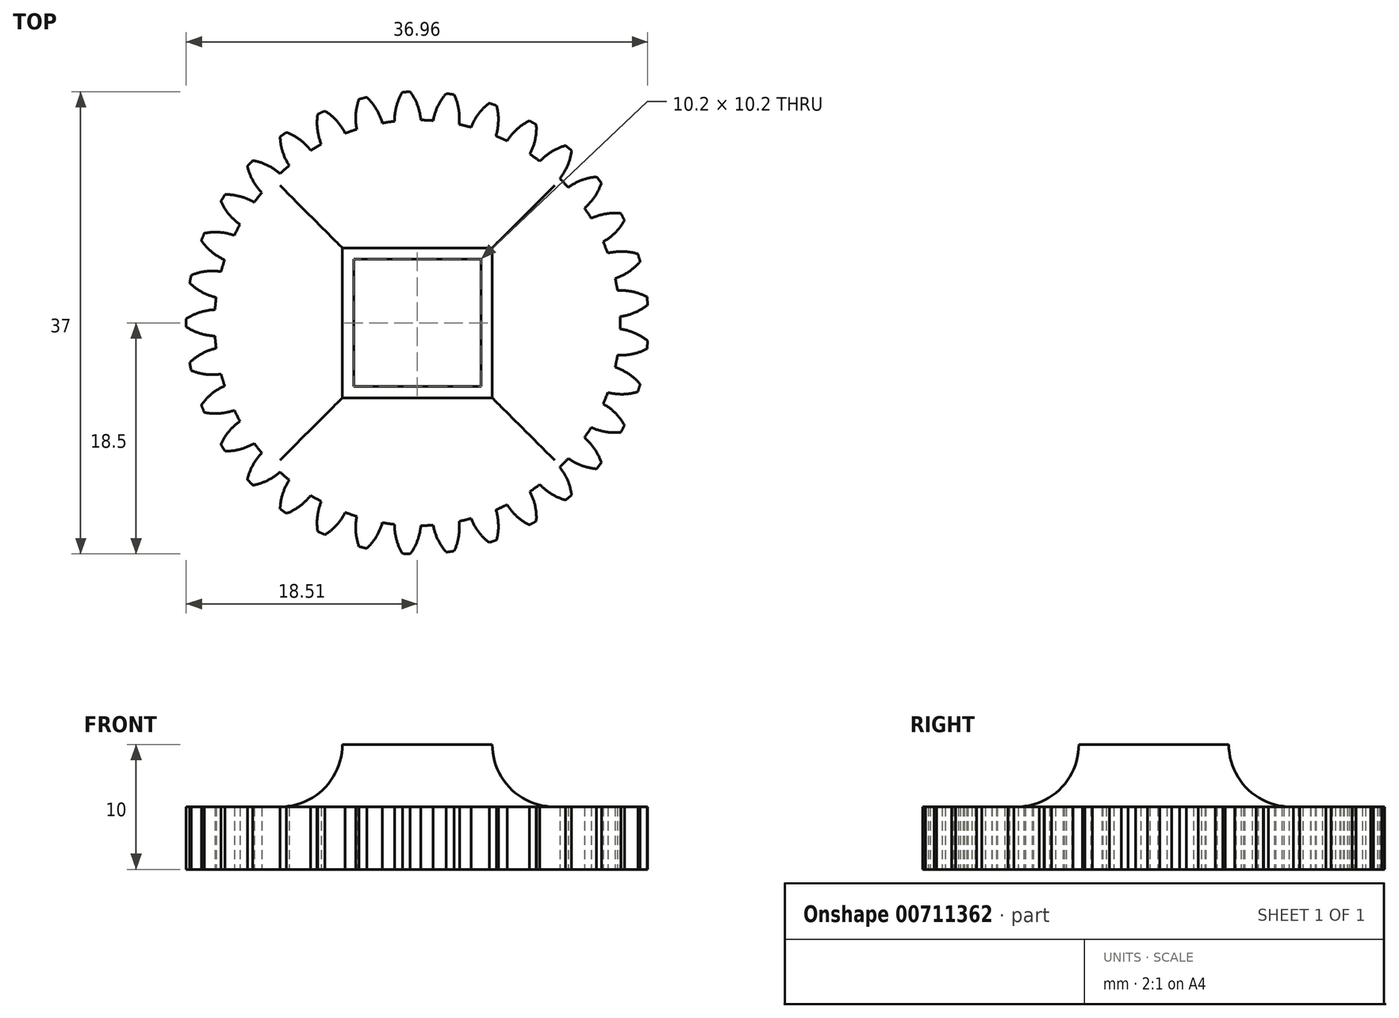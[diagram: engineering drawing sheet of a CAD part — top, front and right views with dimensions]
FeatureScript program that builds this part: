
annotation { "Feature Type Name" : "Feature", "Feature Type Description" : "" }
export const myFeature = defineFeature(function(context is Context, id is Id, definition is map)
    precondition{}
    {
        {
            var Q0;
            Q0=qCreatedBy(makeId("Top.planeOp"),FACE);
            var sketch = newSketch(context, id + "F0", { "sketchPlane" : qUnion([Q0])});
            skCircle(sketch, "E0", {"center": v(0, 0) * mm, "radius": 16.24 * mm});
            skCircle(sketch, "E1", {"center": v(0, 0) * mm, "radius": 17.46 * mm, "construction": true});
            skCircle(sketch, "E2", {"center": v(0, 0) * mm, "radius": 18.52 * mm, "construction": true});
            skLineSegment(sketch, "E3", {"start": v(0, 0) * mm, "end": v(0, 50.63) * mm, "construction": true});
            skLineSegment(sketch, "E4", {"start": v(0, 0) * mm, "end": v(-2.48, 52.12) * mm, "construction": true});
            skLineSegment(sketch, "E5", {"start": v(0, 17.46) * mm, "end": v(-26.32, 17.46) * mm, "construction": true});
            skLineSegment(sketch, "E6", {"start": v(0, 17.46) * mm, "end": v(-24.25, 8.64) * mm, "construction": true});
            skCircle(sketch, "E7", {"center": v(0, 0) * mm, "radius": 16.4 * mm, "construction": true});
            skCircle(sketch, "E8", {"center": v(0, 17.46) * mm, "radius": 4.37 * mm, "construction": true});
            skCircle(sketch, "E9", {"center": v(-4.07, 15.9) * mm, "radius": 4.37 * mm, "construction": true});
            skArc(sketch, "E10", {"start": v(0, 17.46) * mm, "mid": v(-0.25, 18) * mm, "end": v(-0.57, 18.5) * mm});
            skArc(sketch, "E11", {"start": v(0.28, 16.23) * mm, "mid": v(0.18, 16.85) * mm, "end": v(0, 17.46) * mm});
            skCircle(sketch, "E12.MirrorC", {"center": v(2.54, 16.21) * mm, "radius": 4.37 * mm, "construction": true});
            skArc(sketch, "E13.MirrorCS", {"start": v(-1.66, 17.38) * mm, "mid": v(-1.46, 17.94) * mm, "end": v(-1.2, 18.47) * mm});
            skArc(sketch, "E14.MirrorCS", {"start": v(-1.82, 16.13) * mm, "mid": v(-1.79, 16.76) * mm, "end": v(-1.66, 17.38) * mm});
            skArc(sketch, "E15", {"start": v(-0.57, 18.5) * mm, "mid": v(-0.88, 18.48) * mm, "end": v(-1.2, 18.47) * mm});
            skSolve(sketch);
        }
        {
            var Q0;
            {var subQ0=sQuery(id+"F0.wireOp",EDGE,"E0");var subQ1=makeQuery(id+"F0.imprint","INTERSECT",VERTEX,{"derivedFrom":[subQ0,sQuery(id+"F0.wireOp",EDGE,"E11")]});Q0=makeQuery(id+"F0.imprint","IMPRINT",FACE,{"disambiguationData":[TD([[makeQuery(id+"F0.imprint","IMPRINT",EDGE,{"disambiguationData":[TD([[subQ1,-1.0]])],"derivedFrom":subQ0}),1.0]])]});}
            var Q1;
            {var subQ2=sQuery(id+"F0.wireOp",EDGE,"E10");Q1=makeQuery(id+"F0.imprint","IMPRINT",FACE,{"disambiguationData":[TD([[makeQuery(id+"F0.imprint","IMPRINT",EDGE,{"derivedFrom":subQ2}),1.0]])]});}
            extrude(context, id + "F1", {"entities" : qUnion([Q0, Q1]), "depth" : 5 * mm, "offsetDistance" : 25 * mm});
        }
        {
            var Q0;
            Q0=makeQuery(id+"F1.opExtrude","SWEPT_BODY",BODY,{"disambiguationData":[OSD([sQuery(id+"F0.wireOp",EDGE,"E0"),sQuery(id+"F0.wireOp",EDGE,"E10"),sQuery(id+"F0.wireOp",EDGE,"E11"),sQuery(id+"F0.wireOp",EDGE,"E13.MirrorCS"),sQuery(id+"F0.wireOp",EDGE,"E14.MirrorCS"),sQuery(id+"F0.wireOp",EDGE,"E15")])]});
            var Q1;
            Q1=makeQuery(id+"F1.opExtrude","SWEPT_FACE",FACE,{"disambiguationData":[OSD([sQuery(id+"F0.wireOp",EDGE,"E0")])]});
            circularPattern(context, id + "F2", {"entities" : qUnion([Q0]), "axis" : qUnion([Q1]), "angle" : 360 * degree, "instanceCount" : 33, "equalSpace" : true});
        }
        {
            var Q0;
            Q0=makeQuery(id+"F1.opExtrude","CAP_FACE",FACE,{"disambiguationData":[OSD([sQuery(id+"F0.wireOp",EDGE,"E0"),sQuery(id+"F0.wireOp",EDGE,"E10"),sQuery(id+"F0.wireOp",EDGE,"E11"),sQuery(id+"F0.wireOp",EDGE,"E13.MirrorCS"),sQuery(id+"F0.wireOp",EDGE,"E14.MirrorCS"),sQuery(id+"F0.wireOp",EDGE,"E15")])],"isStart":false});
            var sketch = newSketch(context, id + "F3", { "sketchPlane" : qUnion([Q0])});
            skLineSegment(sketch, "E16.bottom", {"start": v(5.1, -5.1) * mm, "end": v(-5.1, -5.1) * mm});
            skLineSegment(sketch, "E16.top", {"start": v(5.1, 5.1) * mm, "end": v(-5.1, 5.1) * mm});
            skLineSegment(sketch, "E16.left", {"start": v(5.1, -5.1) * mm, "end": v(5.1, 5.1) * mm});
            skLineSegment(sketch, "E16.right", {"start": v(-5.1, -5.1) * mm, "end": v(-5.1, 5.1) * mm});
            skPoint(sketch, "E16.middle", {"position": v(0, 0) * mm});
            skLineSegment(sketch, "E17.bottom", {"start": v(6, -6) * mm, "end": v(-6, -6) * mm});
            skLineSegment(sketch, "E17.top", {"start": v(6, 6) * mm, "end": v(-6, 6) * mm});
            skLineSegment(sketch, "E17.left", {"start": v(6, -6) * mm, "end": v(6, 6) * mm});
            skLineSegment(sketch, "E17.right", {"start": v(-6, -6) * mm, "end": v(-6, 6) * mm});
            skSolve(sketch);
        }
        {
            var Q0;
            Q0=makeQuery(id+"F3.imprint","IMPRINT",FACE,{"disambiguationData":[TD([[makeQuery(id+"F3.imprint","IMPRINT",EDGE,{"derivedFrom":sQuery(id+"F3.wireOp",EDGE,"E16.bottom")}),-1.0]])]});
            extrude(context, id + "F4", {"entities" : qUnion([Q0]), "operationType" : NewBodyOperationType.REMOVE, "oppositeDirection" : true, "depth" : 6 * mm, "offsetDistance" : 25 * mm});
        }
        {
            var Q0;
            Q0=makeQuery(id+"F3.imprint","IMPRINT",FACE,{"disambiguationData":[TD([[makeQuery(id+"F3.imprint","IMPRINT",EDGE,{"derivedFrom":sQuery(id+"F3.wireOp",EDGE,"E16.bottom")}),1.0]])]});
            extrude(context, id + "F5", {"entities" : qUnion([Q0]), "operationType" : NewBodyOperationType.ADD, "depth" : 5 * mm, "offsetDistance" : 25 * mm});
        }
        {
            var Q0;
            {var subQ0=makeQuery(id+"F1.opExtrude","CAP_FACE",FACE,{"disambiguationData":[OSD([sQuery(id+"F0.wireOp",EDGE,"E0"),sQuery(id+"F0.wireOp",EDGE,"E10"),sQuery(id+"F0.wireOp",EDGE,"E11"),sQuery(id+"F0.wireOp",EDGE,"E13.MirrorCS"),sQuery(id+"F0.wireOp",EDGE,"E14.MirrorCS"),sQuery(id+"F0.wireOp",EDGE,"E15")])],"isStart":false});var subQ1=makeQuery(id+"F2.opPattern","COPY",FACE,{"derivedFrom":subQ0,"instanceName":"21"});var subQ2=makeQuery(id+"F2.opPattern","COPY",FACE,{"derivedFrom":subQ0,"instanceName":"19"});var subQ3=makeQuery(id+"F2.opPattern","COPY",FACE,{"derivedFrom":subQ0,"instanceName":"18"});var subQ4=makeQuery(id+"F2.opPattern","COPY",FACE,{"derivedFrom":subQ0,"instanceName":"17"});var subQ5=makeQuery(id+"F2.opPattern","COPY",FACE,{"derivedFrom":subQ0,"instanceName":"16"});var subQ6=makeQuery(id+"F2.opPattern","COPY",FACE,{"derivedFrom":subQ0,"instanceName":"15"});var subQ7=makeQuery(id+"F2.opPattern","COPY",FACE,{"derivedFrom":subQ0,"instanceName":"14"});var subQ8=makeQuery(id+"F2.opPattern","COPY",FACE,{"derivedFrom":subQ0,"instanceName":"13"});var subQ9=makeQuery(id+"F2.opPattern","COPY",FACE,{"derivedFrom":subQ0,"instanceName":"12"});var subQ10=makeQuery(id+"F2.opPattern","COPY",FACE,{"derivedFrom":subQ0,"instanceName":"11"});var subQ11=makeQuery(id+"F2.opPattern","COPY",FACE,{"derivedFrom":subQ0,"instanceName":"10"});var subQ12=makeQuery(id+"F2.opPattern","COPY",FACE,{"derivedFrom":subQ0,"instanceName":"3"});var subQ13=makeQuery(id+"F2.opPattern","COPY",FACE,{"derivedFrom":subQ0,"instanceName":"2"});var subQ14=makeQuery(id+"F2.opPattern","COPY",FACE,{"derivedFrom":subQ0,"instanceName":"1"});var subQ15=makeQuery(id+"F2.opPattern","COPY",FACE,{"derivedFrom":subQ0,"instanceName":"20"});var subQ16=makeQuery(id+"F2.opPattern","COPY",FACE,{"derivedFrom":subQ0,"instanceName":"6"});var subQ17=makeQuery(id+"F2.opPattern","COPY",FACE,{"derivedFrom":subQ0,"instanceName":"4"});var subQ18=makeQuery(id+"F2.opPattern","COPY",FACE,{"derivedFrom":subQ0,"instanceName":"5"});var subQ19=makeQuery(id+"F2.opPattern","COPY",FACE,{"derivedFrom":subQ0,"instanceName":"7"});var subQ20=makeQuery(id+"F2.opPattern","COPY",FACE,{"derivedFrom":subQ0,"instanceName":"8"});var subQ21=makeQuery(id+"F2.opPattern","COPY",FACE,{"derivedFrom":subQ0,"instanceName":"9"});var subQ22=makeQuery(id+"F2.opPattern","COPY",FACE,{"derivedFrom":subQ0,"instanceName":"22"});var subQ23=makeQuery(id+"F2.opPattern","COPY",FACE,{"derivedFrom":subQ0,"instanceName":"23"});var subQ24=makeQuery(id+"F2.opPattern","COPY",FACE,{"derivedFrom":subQ0,"instanceName":"24"});var subQ25=makeQuery(id+"F2.opPattern","COPY",FACE,{"derivedFrom":subQ0,"instanceName":"25"});var subQ26=makeQuery(id+"F2.opPattern","COPY",FACE,{"derivedFrom":subQ0,"instanceName":"26"});var subQ27=makeQuery(id+"F2.opPattern","COPY",FACE,{"derivedFrom":subQ0,"instanceName":"27"});var subQ28=makeQuery(id+"F2.opPattern","COPY",FACE,{"derivedFrom":subQ0,"instanceName":"28"});var subQ29=makeQuery(id+"F2.opPattern","COPY",FACE,{"derivedFrom":subQ0,"instanceName":"29"});var subQ30=makeQuery(id+"F2.opPattern","COPY",FACE,{"derivedFrom":subQ0,"instanceName":"30"});var subQ31=makeQuery(id+"F2.opPattern","COPY",FACE,{"derivedFrom":subQ0,"instanceName":"31"});var subQ32=makeQuery(id+"F2.opPattern","COPY",FACE,{"derivedFrom":subQ0,"instanceName":"32"});Q0=makeQuery(id+"F5.boolean.opBoolean","INTERSECT",EDGE,{"disambiguationData":[topologyDisambiguationEdgeConnected([makeQuery(id+"F5.opExtrude","SWEPT_FACE",FACE,{"disambiguationData":[OSD([sQuery(id+"F3.wireOp",EDGE,"E17.right")])]})])],"derivedFrom":[subQ0,subQ14,subQ13,subQ12,subQ17,subQ18,subQ16,subQ19,subQ20,subQ21,subQ11,subQ10,subQ9,subQ8,subQ7,subQ6,subQ5,subQ4,subQ3,subQ2,subQ15,subQ1,subQ22,subQ23,subQ24,subQ25,subQ26,subQ27,subQ28,subQ29,subQ30,subQ31,subQ32]});}
            var Q1;
            {var subQ0=makeQuery(id+"F1.opExtrude","CAP_FACE",FACE,{"disambiguationData":[OSD([sQuery(id+"F0.wireOp",EDGE,"E0"),sQuery(id+"F0.wireOp",EDGE,"E10"),sQuery(id+"F0.wireOp",EDGE,"E11"),sQuery(id+"F0.wireOp",EDGE,"E13.MirrorCS"),sQuery(id+"F0.wireOp",EDGE,"E14.MirrorCS"),sQuery(id+"F0.wireOp",EDGE,"E15")])],"isStart":false});var subQ1=makeQuery(id+"F2.opPattern","COPY",FACE,{"derivedFrom":subQ0,"instanceName":"21"});var subQ2=makeQuery(id+"F2.opPattern","COPY",FACE,{"derivedFrom":subQ0,"instanceName":"19"});var subQ3=makeQuery(id+"F2.opPattern","COPY",FACE,{"derivedFrom":subQ0,"instanceName":"18"});var subQ4=makeQuery(id+"F2.opPattern","COPY",FACE,{"derivedFrom":subQ0,"instanceName":"17"});var subQ5=makeQuery(id+"F2.opPattern","COPY",FACE,{"derivedFrom":subQ0,"instanceName":"16"});var subQ6=makeQuery(id+"F2.opPattern","COPY",FACE,{"derivedFrom":subQ0,"instanceName":"15"});var subQ7=makeQuery(id+"F2.opPattern","COPY",FACE,{"derivedFrom":subQ0,"instanceName":"14"});var subQ8=makeQuery(id+"F2.opPattern","COPY",FACE,{"derivedFrom":subQ0,"instanceName":"13"});var subQ9=makeQuery(id+"F2.opPattern","COPY",FACE,{"derivedFrom":subQ0,"instanceName":"12"});var subQ10=makeQuery(id+"F2.opPattern","COPY",FACE,{"derivedFrom":subQ0,"instanceName":"11"});var subQ11=makeQuery(id+"F2.opPattern","COPY",FACE,{"derivedFrom":subQ0,"instanceName":"10"});var subQ12=makeQuery(id+"F2.opPattern","COPY",FACE,{"derivedFrom":subQ0,"instanceName":"3"});var subQ13=makeQuery(id+"F2.opPattern","COPY",FACE,{"derivedFrom":subQ0,"instanceName":"2"});var subQ14=makeQuery(id+"F2.opPattern","COPY",FACE,{"derivedFrom":subQ0,"instanceName":"1"});var subQ15=makeQuery(id+"F2.opPattern","COPY",FACE,{"derivedFrom":subQ0,"instanceName":"20"});var subQ16=makeQuery(id+"F2.opPattern","COPY",FACE,{"derivedFrom":subQ0,"instanceName":"6"});var subQ17=makeQuery(id+"F2.opPattern","COPY",FACE,{"derivedFrom":subQ0,"instanceName":"4"});var subQ18=makeQuery(id+"F2.opPattern","COPY",FACE,{"derivedFrom":subQ0,"instanceName":"5"});var subQ19=makeQuery(id+"F2.opPattern","COPY",FACE,{"derivedFrom":subQ0,"instanceName":"7"});var subQ20=makeQuery(id+"F2.opPattern","COPY",FACE,{"derivedFrom":subQ0,"instanceName":"8"});var subQ21=makeQuery(id+"F2.opPattern","COPY",FACE,{"derivedFrom":subQ0,"instanceName":"9"});var subQ22=makeQuery(id+"F2.opPattern","COPY",FACE,{"derivedFrom":subQ0,"instanceName":"22"});var subQ23=makeQuery(id+"F2.opPattern","COPY",FACE,{"derivedFrom":subQ0,"instanceName":"23"});var subQ24=makeQuery(id+"F2.opPattern","COPY",FACE,{"derivedFrom":subQ0,"instanceName":"24"});var subQ25=makeQuery(id+"F2.opPattern","COPY",FACE,{"derivedFrom":subQ0,"instanceName":"25"});var subQ26=makeQuery(id+"F2.opPattern","COPY",FACE,{"derivedFrom":subQ0,"instanceName":"26"});var subQ27=makeQuery(id+"F2.opPattern","COPY",FACE,{"derivedFrom":subQ0,"instanceName":"27"});var subQ28=makeQuery(id+"F2.opPattern","COPY",FACE,{"derivedFrom":subQ0,"instanceName":"28"});var subQ29=makeQuery(id+"F2.opPattern","COPY",FACE,{"derivedFrom":subQ0,"instanceName":"29"});var subQ30=makeQuery(id+"F2.opPattern","COPY",FACE,{"derivedFrom":subQ0,"instanceName":"30"});var subQ31=makeQuery(id+"F2.opPattern","COPY",FACE,{"derivedFrom":subQ0,"instanceName":"31"});var subQ32=makeQuery(id+"F2.opPattern","COPY",FACE,{"derivedFrom":subQ0,"instanceName":"32"});Q1=makeQuery(id+"F5.boolean.opBoolean","INTERSECT",EDGE,{"disambiguationData":[topologyDisambiguationEdgeConnected([makeQuery(id+"F5.opExtrude","SWEPT_FACE",FACE,{"disambiguationData":[OSD([sQuery(id+"F3.wireOp",EDGE,"E17.top")])]})])],"derivedFrom":[subQ0,subQ14,subQ13,subQ12,subQ17,subQ18,subQ16,subQ19,subQ20,subQ21,subQ11,subQ10,subQ9,subQ8,subQ7,subQ6,subQ5,subQ4,subQ3,subQ2,subQ15,subQ1,subQ22,subQ23,subQ24,subQ25,subQ26,subQ27,subQ28,subQ29,subQ30,subQ31,subQ32]});}
            var Q2;
            {var subQ0=makeQuery(id+"F1.opExtrude","CAP_FACE",FACE,{"disambiguationData":[OSD([sQuery(id+"F0.wireOp",EDGE,"E0"),sQuery(id+"F0.wireOp",EDGE,"E10"),sQuery(id+"F0.wireOp",EDGE,"E11"),sQuery(id+"F0.wireOp",EDGE,"E13.MirrorCS"),sQuery(id+"F0.wireOp",EDGE,"E14.MirrorCS"),sQuery(id+"F0.wireOp",EDGE,"E15")])],"isStart":false});var subQ1=makeQuery(id+"F2.opPattern","COPY",FACE,{"derivedFrom":subQ0,"instanceName":"21"});var subQ2=makeQuery(id+"F2.opPattern","COPY",FACE,{"derivedFrom":subQ0,"instanceName":"19"});var subQ3=makeQuery(id+"F2.opPattern","COPY",FACE,{"derivedFrom":subQ0,"instanceName":"18"});var subQ4=makeQuery(id+"F2.opPattern","COPY",FACE,{"derivedFrom":subQ0,"instanceName":"17"});var subQ5=makeQuery(id+"F2.opPattern","COPY",FACE,{"derivedFrom":subQ0,"instanceName":"16"});var subQ6=makeQuery(id+"F2.opPattern","COPY",FACE,{"derivedFrom":subQ0,"instanceName":"15"});var subQ7=makeQuery(id+"F2.opPattern","COPY",FACE,{"derivedFrom":subQ0,"instanceName":"14"});var subQ8=makeQuery(id+"F2.opPattern","COPY",FACE,{"derivedFrom":subQ0,"instanceName":"13"});var subQ9=makeQuery(id+"F2.opPattern","COPY",FACE,{"derivedFrom":subQ0,"instanceName":"12"});var subQ10=makeQuery(id+"F2.opPattern","COPY",FACE,{"derivedFrom":subQ0,"instanceName":"11"});var subQ11=makeQuery(id+"F2.opPattern","COPY",FACE,{"derivedFrom":subQ0,"instanceName":"10"});var subQ12=makeQuery(id+"F2.opPattern","COPY",FACE,{"derivedFrom":subQ0,"instanceName":"3"});var subQ13=makeQuery(id+"F2.opPattern","COPY",FACE,{"derivedFrom":subQ0,"instanceName":"2"});var subQ14=makeQuery(id+"F2.opPattern","COPY",FACE,{"derivedFrom":subQ0,"instanceName":"1"});var subQ15=makeQuery(id+"F2.opPattern","COPY",FACE,{"derivedFrom":subQ0,"instanceName":"20"});var subQ16=makeQuery(id+"F2.opPattern","COPY",FACE,{"derivedFrom":subQ0,"instanceName":"6"});var subQ17=makeQuery(id+"F2.opPattern","COPY",FACE,{"derivedFrom":subQ0,"instanceName":"4"});var subQ18=makeQuery(id+"F2.opPattern","COPY",FACE,{"derivedFrom":subQ0,"instanceName":"5"});var subQ19=makeQuery(id+"F2.opPattern","COPY",FACE,{"derivedFrom":subQ0,"instanceName":"7"});var subQ20=makeQuery(id+"F2.opPattern","COPY",FACE,{"derivedFrom":subQ0,"instanceName":"8"});var subQ21=makeQuery(id+"F2.opPattern","COPY",FACE,{"derivedFrom":subQ0,"instanceName":"9"});var subQ22=makeQuery(id+"F2.opPattern","COPY",FACE,{"derivedFrom":subQ0,"instanceName":"22"});var subQ23=makeQuery(id+"F2.opPattern","COPY",FACE,{"derivedFrom":subQ0,"instanceName":"23"});var subQ24=makeQuery(id+"F2.opPattern","COPY",FACE,{"derivedFrom":subQ0,"instanceName":"24"});var subQ25=makeQuery(id+"F2.opPattern","COPY",FACE,{"derivedFrom":subQ0,"instanceName":"25"});var subQ26=makeQuery(id+"F2.opPattern","COPY",FACE,{"derivedFrom":subQ0,"instanceName":"26"});var subQ27=makeQuery(id+"F2.opPattern","COPY",FACE,{"derivedFrom":subQ0,"instanceName":"27"});var subQ28=makeQuery(id+"F2.opPattern","COPY",FACE,{"derivedFrom":subQ0,"instanceName":"28"});var subQ29=makeQuery(id+"F2.opPattern","COPY",FACE,{"derivedFrom":subQ0,"instanceName":"29"});var subQ30=makeQuery(id+"F2.opPattern","COPY",FACE,{"derivedFrom":subQ0,"instanceName":"30"});var subQ31=makeQuery(id+"F2.opPattern","COPY",FACE,{"derivedFrom":subQ0,"instanceName":"31"});var subQ32=makeQuery(id+"F2.opPattern","COPY",FACE,{"derivedFrom":subQ0,"instanceName":"32"});Q2=makeQuery(id+"F5.boolean.opBoolean","INTERSECT",EDGE,{"disambiguationData":[topologyDisambiguationEdgeConnected([makeQuery(id+"F5.opExtrude","SWEPT_FACE",FACE,{"disambiguationData":[OSD([sQuery(id+"F3.wireOp",EDGE,"E17.left")])]})])],"derivedFrom":[subQ0,subQ14,subQ13,subQ12,subQ17,subQ18,subQ16,subQ19,subQ20,subQ21,subQ11,subQ10,subQ9,subQ8,subQ7,subQ6,subQ5,subQ4,subQ3,subQ2,subQ15,subQ1,subQ22,subQ23,subQ24,subQ25,subQ26,subQ27,subQ28,subQ29,subQ30,subQ31,subQ32]});}
            var Q3;
            {var subQ0=makeQuery(id+"F1.opExtrude","CAP_FACE",FACE,{"disambiguationData":[OSD([sQuery(id+"F0.wireOp",EDGE,"E0"),sQuery(id+"F0.wireOp",EDGE,"E10"),sQuery(id+"F0.wireOp",EDGE,"E11"),sQuery(id+"F0.wireOp",EDGE,"E13.MirrorCS"),sQuery(id+"F0.wireOp",EDGE,"E14.MirrorCS"),sQuery(id+"F0.wireOp",EDGE,"E15")])],"isStart":false});var subQ1=makeQuery(id+"F2.opPattern","COPY",FACE,{"derivedFrom":subQ0,"instanceName":"21"});var subQ2=makeQuery(id+"F2.opPattern","COPY",FACE,{"derivedFrom":subQ0,"instanceName":"19"});var subQ3=makeQuery(id+"F2.opPattern","COPY",FACE,{"derivedFrom":subQ0,"instanceName":"18"});var subQ4=makeQuery(id+"F2.opPattern","COPY",FACE,{"derivedFrom":subQ0,"instanceName":"17"});var subQ5=makeQuery(id+"F2.opPattern","COPY",FACE,{"derivedFrom":subQ0,"instanceName":"16"});var subQ6=makeQuery(id+"F2.opPattern","COPY",FACE,{"derivedFrom":subQ0,"instanceName":"15"});var subQ7=makeQuery(id+"F2.opPattern","COPY",FACE,{"derivedFrom":subQ0,"instanceName":"14"});var subQ8=makeQuery(id+"F2.opPattern","COPY",FACE,{"derivedFrom":subQ0,"instanceName":"13"});var subQ9=makeQuery(id+"F2.opPattern","COPY",FACE,{"derivedFrom":subQ0,"instanceName":"12"});var subQ10=makeQuery(id+"F2.opPattern","COPY",FACE,{"derivedFrom":subQ0,"instanceName":"11"});var subQ11=makeQuery(id+"F2.opPattern","COPY",FACE,{"derivedFrom":subQ0,"instanceName":"10"});var subQ12=makeQuery(id+"F2.opPattern","COPY",FACE,{"derivedFrom":subQ0,"instanceName":"3"});var subQ13=makeQuery(id+"F2.opPattern","COPY",FACE,{"derivedFrom":subQ0,"instanceName":"2"});var subQ14=makeQuery(id+"F2.opPattern","COPY",FACE,{"derivedFrom":subQ0,"instanceName":"1"});var subQ15=makeQuery(id+"F2.opPattern","COPY",FACE,{"derivedFrom":subQ0,"instanceName":"20"});var subQ16=makeQuery(id+"F2.opPattern","COPY",FACE,{"derivedFrom":subQ0,"instanceName":"6"});var subQ17=makeQuery(id+"F2.opPattern","COPY",FACE,{"derivedFrom":subQ0,"instanceName":"4"});var subQ18=makeQuery(id+"F2.opPattern","COPY",FACE,{"derivedFrom":subQ0,"instanceName":"5"});var subQ19=makeQuery(id+"F2.opPattern","COPY",FACE,{"derivedFrom":subQ0,"instanceName":"7"});var subQ20=makeQuery(id+"F2.opPattern","COPY",FACE,{"derivedFrom":subQ0,"instanceName":"8"});var subQ21=makeQuery(id+"F2.opPattern","COPY",FACE,{"derivedFrom":subQ0,"instanceName":"9"});var subQ22=makeQuery(id+"F2.opPattern","COPY",FACE,{"derivedFrom":subQ0,"instanceName":"22"});var subQ23=makeQuery(id+"F2.opPattern","COPY",FACE,{"derivedFrom":subQ0,"instanceName":"23"});var subQ24=makeQuery(id+"F2.opPattern","COPY",FACE,{"derivedFrom":subQ0,"instanceName":"24"});var subQ25=makeQuery(id+"F2.opPattern","COPY",FACE,{"derivedFrom":subQ0,"instanceName":"25"});var subQ26=makeQuery(id+"F2.opPattern","COPY",FACE,{"derivedFrom":subQ0,"instanceName":"26"});var subQ27=makeQuery(id+"F2.opPattern","COPY",FACE,{"derivedFrom":subQ0,"instanceName":"27"});var subQ28=makeQuery(id+"F2.opPattern","COPY",FACE,{"derivedFrom":subQ0,"instanceName":"28"});var subQ29=makeQuery(id+"F2.opPattern","COPY",FACE,{"derivedFrom":subQ0,"instanceName":"29"});var subQ30=makeQuery(id+"F2.opPattern","COPY",FACE,{"derivedFrom":subQ0,"instanceName":"30"});var subQ31=makeQuery(id+"F2.opPattern","COPY",FACE,{"derivedFrom":subQ0,"instanceName":"31"});var subQ32=makeQuery(id+"F2.opPattern","COPY",FACE,{"derivedFrom":subQ0,"instanceName":"32"});Q3=makeQuery(id+"F5.boolean.opBoolean","INTERSECT",EDGE,{"disambiguationData":[topologyDisambiguationEdgeConnected([makeQuery(id+"F5.opExtrude","SWEPT_FACE",FACE,{"disambiguationData":[OSD([sQuery(id+"F3.wireOp",EDGE,"E17.bottom")])]})])],"derivedFrom":[subQ0,subQ14,subQ13,subQ12,subQ17,subQ18,subQ16,subQ19,subQ20,subQ21,subQ11,subQ10,subQ9,subQ8,subQ7,subQ6,subQ5,subQ4,subQ3,subQ2,subQ15,subQ1,subQ22,subQ23,subQ24,subQ25,subQ26,subQ27,subQ28,subQ29,subQ30,subQ31,subQ32]});}
            fillet(context, id + "F6", {"entities" : qUnion([Q0, Q1, Q2, Q3]), "radius" : 5 * mm, "tangentPropagation" : true, "allowEdgeOverflow" : false});
        }
    });
